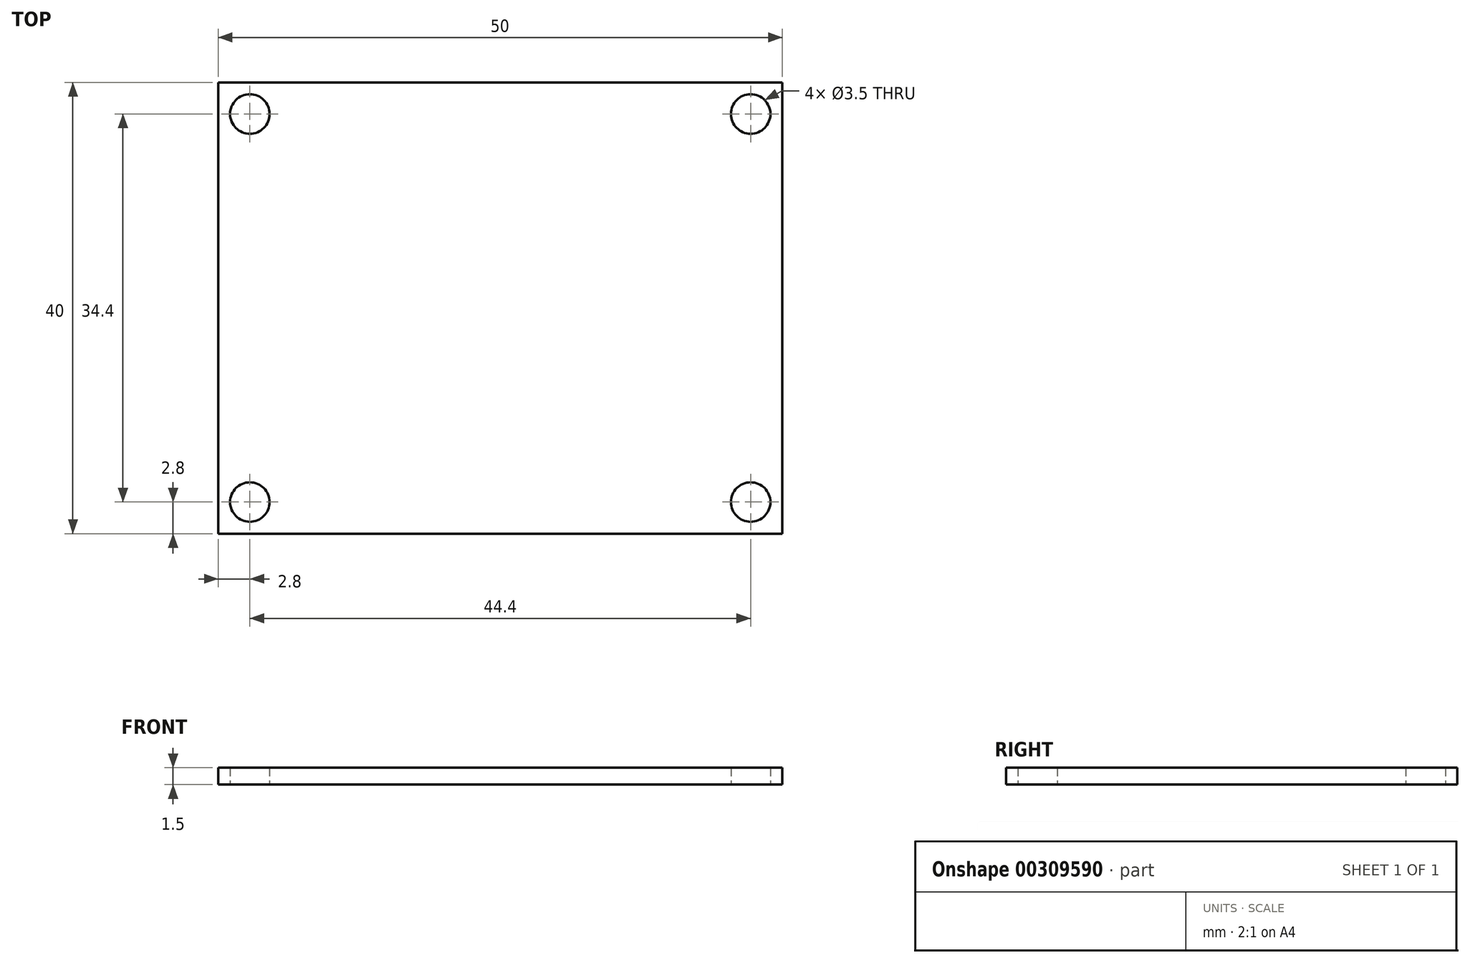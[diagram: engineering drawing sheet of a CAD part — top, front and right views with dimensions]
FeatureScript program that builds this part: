
annotation { "Feature Type Name" : "Feature", "Feature Type Description" : "" }
export const myFeature = defineFeature(function(context is Context, id is Id, definition is map)
    precondition{}
    {
        {
            assignVariable(context, id + "F0", {"name" : "PCB_T", "anyValue" : 1.5});
        }
        {
            assignVariable(context, id + "F1", {"name" : "HOLE_DIA", "anyValue" : 3.5});
        }
        {
            var Q0;
            Q0=qCreatedBy(makeId("Top.planeOp"),FACE);
            var sketch = newSketch(context, id + "F2", { "sketchPlane" : qUnion([Q0])});
            skLineSegment(sketch, "E0.bottom", {"start": v(25, -20) * mm, "end": v(-25, -20) * mm});
            skLineSegment(sketch, "E0.top", {"start": v(25, 20) * mm, "end": v(-25, 20) * mm});
            skLineSegment(sketch, "E0.left", {"start": v(25, -20) * mm, "end": v(25, 20) * mm});
            skLineSegment(sketch, "E0.right", {"start": v(-25, -20) * mm, "end": v(-25, 20) * mm});
            skPoint(sketch, "E0.middle", {"position": v(0, 0) * mm});
            skPoint(sketch, "E1", {"position": v(-22.2, 17.2) * mm});
            skPoint(sketch, "E2", {"position": v(-22.2, -17.2) * mm});
            skPoint(sketch, "E3", {"position": v(22.2, -17.2) * mm});
            skPoint(sketch, "E4", {"position": v(22.2, 17.2) * mm});
            skSolve(sketch);
        }
        {
            var Q0;
            Q0=makeQuery(id+"F2.imprint","IMPRINT",FACE,{"disambiguationData":[TD([[makeQuery(id+"F2.imprint","IMPRINT",EDGE,{"derivedFrom":sQuery(id+"F2.wireOp",EDGE,"E0.bottom")}),-1.0]])]});
            extrude(context, id + "F3", {"entities" : qUnion([Q0]), "depth" : (getVariable(context, 'PCB_T')) * mm, "offsetDistance" : 25 * mm});
        }
        {
            var Q0;
            Q0=sQuery(id+"F2.wireOp",VERTEX,"E2");
            var Q1;
            Q1=sQuery(id+"F2.wireOp",VERTEX,"E1");
            var Q2;
            Q2=sQuery(id+"F2.wireOp",VERTEX,"E3");
            var Q3;
            Q3=sQuery(id+"F2.wireOp",VERTEX,"E4");
            var Q4;
            Q4=makeQuery(id+"F3.opExtrude","SWEPT_BODY",BODY,{"disambiguationData":[OSD([sQuery(id+"F2.wireOp",EDGE,"E0.bottom"),sQuery(id+"F2.wireOp",EDGE,"E0.top"),sQuery(id+"F2.wireOp",EDGE,"E0.left"),sQuery(id+"F2.wireOp",EDGE,"E0.right")])]});
            hole(context, id + "F4", {"style" : HoleStyle.SIMPLE, "endStyle" : HoleEndStyle.THROUGH, "oppositeDirection" : true, "holeDiameter" : (getVariable(context, 'HOLE_DIA')) * mm, "majorDiameter" : 5 * mm, "isTappedThrough" : true, "tappedDepth" : 12 * mm, "tapClearance" : 3, "startFromSketch" : true, "locations" : qUnion([Q0, Q1, Q2, Q3]), "scope" : qUnion([Q4])});
        }
    });
